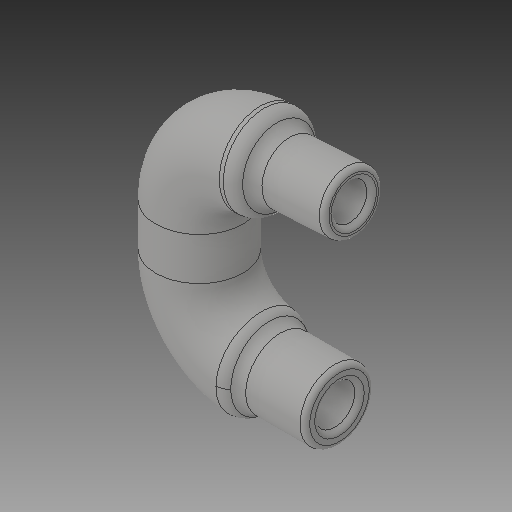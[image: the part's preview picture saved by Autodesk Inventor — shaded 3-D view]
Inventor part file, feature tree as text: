
AUTODESK INVENTOR PART (.ipt)
format: ipt  version: 2019 (Build 230136000, 136)  size: 321,024 bytes
history: native  units: in
note: dims shown in document units (in); Inventor stores cm internally (conversion verified against a paired STEP export)
features: sketch x6, extrude x5, sweep x4, plane x2, fillet x2, projected_geometry x1
ambient origin geometry x8: Origin, YZ Plane, XZ Plane, XY Plane, X Axis, Y Axis, Z Axis, Center Point
bodies: Solid1 (feature_tree)
feature tree (20):
  sketch  "Sketch2"  dims[d0=0.0in d1=0.0in d4=0.1575in]
  plane  "Work Plane1"
  sketch  "Sketch3"  dims[d11=0.2953in d12=0.2953in]
  sweep  "Sweep1"
  sweep  "Sweep11"
  extrude  "Extrusion10"  Depth=0.2756in
  sketch  "Sketch11"  dims[d31=0.2756in d36=0.0754in]
  extrude  "Extrusion11"  Depth=0.2756in
  extrude  "Extrusion12"  Depth=0.2409in
  plane  "Work Plane2"
  sketch  "Sketch12"  dims[d37=0.1457in d43=0.2409in]
  extrude  "Extrusion13"  Depth=0.0197in
  extrude  "Extrusion14"  Depth=0.0197in
  sweep  "Sweep12"
  sweep  "Sweep13"
  fillet  "Fillet3"  Radius=0.2953in
  fillet  "Fillet4"  [1 undecoded]
  sketch  "Sketch10"  dims[d13=0.3543in d30=0.2756in]
  projected_geometry  "Projected Loop3"
  sketch  "Sketch13"  dims[d62=0.0in d63=0.0in d64=0.2815in d65=0.2559in d66=0.0in d67=0.2823in d68=0.2953in d69=0.0in d70=0.2953in d71=0.0117in d72=0.1457in d73=0.1457in d74=0.2756in d75=0.2953in d76=0.0117in d77=0.2953in d78=0.0in d79=0.0in d80=0.0in d81=0.0in d82=0.0in d83=0.0591in d84=0.0197in d85=0.0118in]
note: 1 required parameter value undecoded (feature->parameter linkage not recoverable at this tier; creation-order binding heuristic only, values carry confidence <= 0.55)
